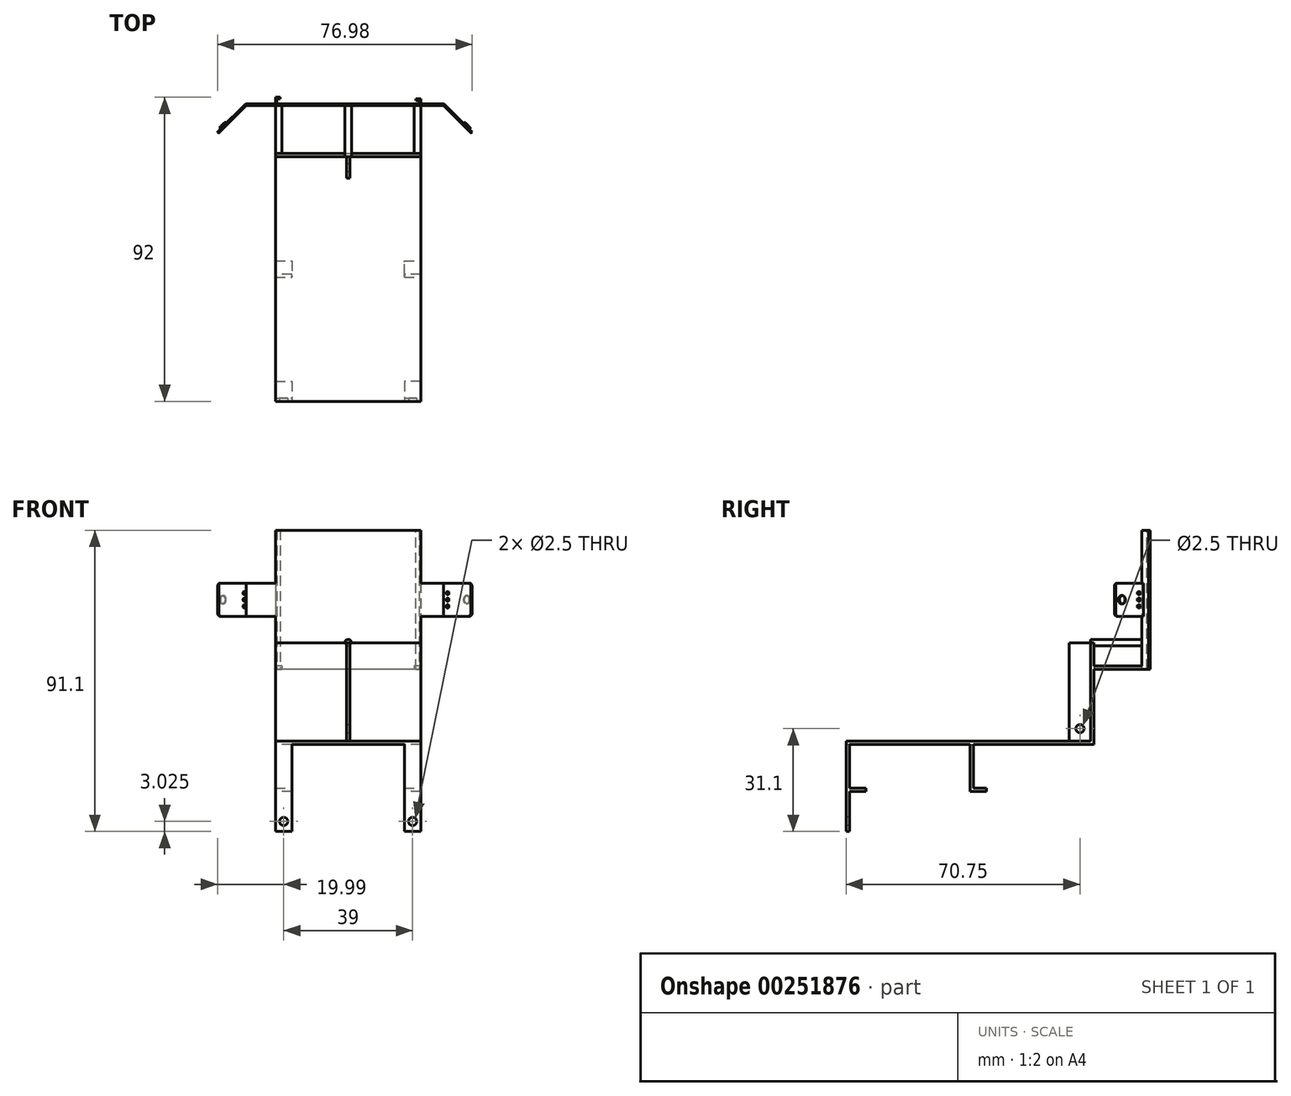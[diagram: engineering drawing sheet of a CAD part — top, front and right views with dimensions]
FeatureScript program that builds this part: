
annotation { "Feature Type Name" : "Feature", "Feature Type Description" : "" }
export const myFeature = defineFeature(function(context is Context, id is Id, definition is map)
    precondition{}
    {
        {
            var Q0;
            Q0=qCreatedBy(makeId("Front.planeOp"),FACE);
            var sketch = newSketch(context, id + "F0", { "sketchPlane" : qUnion([Q0])});
            skLineSegment(sketch, "E0", {"start": v(-30, 5) * mm, "end": v(30, 5) * mm});
            skLineSegment(sketch, "E1", {"start": v(30, 5) * mm, "end": v(30, -5) * mm});
            skLineSegment(sketch, "E2", {"start": v(30, -5) * mm, "end": v(-30, -5) * mm});
            skLineSegment(sketch, "E3", {"start": v(-30, -5) * mm, "end": v(-30, 5) * mm});
            skLineSegment(sketch, "E4", {"start": v(0, 5) * mm, "end": v(-21, 5) * mm, "construction": true});
            skLineSegment(sketch, "E5", {"start": v(-21, 5) * mm, "end": v(-21, 21) * mm, "construction": true});
            skLineSegment(sketch, "E6", {"start": v(-21, 21) * mm, "end": v(23, 21) * mm});
            skLineSegment(sketch, "E7", {"start": v(23, 21) * mm, "end": v(23, -21) * mm});
            skLineSegment(sketch, "E8", {"start": v(23, -21) * mm, "end": v(-21, -21) * mm});
            skLineSegment(sketch, "E9", {"start": v(-21, -21) * mm, "end": v(-21, 21) * mm});
            skPoint(sketch, "E10", {"position": v(0, 0) * mm});
            skLineSegment(sketch, "E11", {"start": v(-21, -21) * mm, "end": v(23, -5) * mm, "construction": true});
            skLineSegment(sketch, "E12", {"start": v(-21, -5) * mm, "end": v(23, -21) * mm, "construction": true});
            skPoint(sketch, "E13", {"position": v(1, -13) * mm});
            skCircle(sketch, "E14", {"center": v(1, -13) * mm, "radius": 1 * mm});
            skSolve(sketch);
        }
        {
            var Q0;
            Q0 = qSketchRegion(id + "F0", true);
            extrude(context, id + "F1", {"entities" : qUnion([Q0]), "depth" : 0.5 * mm});
        }
        {
            var Q0;
            Q0=makeQuery(id+"F1.opExtrude","CAP_EDGE",EDGE,{"disambiguationData":[OSD([sQuery(id+"F0.wireOp",EDGE,"E1")])],"isStart":true});
            var Q1;
            Q1=makeQuery(id+"F1.opExtrude","SWEPT_FACE",FACE,{"disambiguationData":[OSD([sQuery(id+"F0.wireOp",EDGE,"E1")])]});
            cPlane(context, id + "F2", {"entities" : qUnion([Q0, Q1]), "cplaneType" : CPlaneType.LINE_ANGLE, "offset" : 25 * mm, "angle" : 45 * degree, "oppositeDirection" : true, "width" : 150 * mm, "height" : 150 * mm});
        }
        {
            var Q0;
            Q0=qCreatedBy(id+"F2.planeOp",FACE);
            var sketch = newSketch(context, id + "F3", { "sketchPlane" : qUnion([Q0])});
            skLineSegment(sketch, "E15.0.0", {"start": v(21.21, -5) * mm, "end": v(21.21, 5) * mm});
            skLineSegment(sketch, "E15.0.1", {"start": v(21.21, 5) * mm, "end": v(21.57, 5) * mm});
            skLineSegment(sketch, "E15.0.2", {"start": v(21.57, 5) * mm, "end": v(21.57, -5) * mm});
            skLineSegment(sketch, "E15.0.3", {"start": v(21.57, -5) * mm, "end": v(21.21, -5) * mm});
            skLineSegment(sketch, "E16", {"start": v(21.21, -5) * mm, "end": v(32.21, -5) * mm});
            skLineSegment(sketch, "E17", {"start": v(33.21, -4) * mm, "end": v(33.21, 4) * mm});
            skLineSegment(sketch, "E18", {"start": v(32.21, 5) * mm, "end": v(21.21, 5) * mm});
            skPoint(sketch, "E19.visualSharp", {"position": v(33.21, 5) * mm});
            skArc(sketch, "E19.filletArc", {"start": v(33.21, 4) * mm, "mid": v(32.92, 4.7) * mm, "end": v(32.21, 5) * mm});
            skPoint(sketch, "E20.visualSharp", {"position": v(21.21, 5) * mm});
            skLineSegment(sketch, "E20.filletArc", {"start": v(21.21, 5) * mm, "end": v(21.21, 5) * mm});
            skPoint(sketch, "E21.visualSharp", {"position": v(21.21, -5) * mm});
            skLineSegment(sketch, "E21.filletArc", {"start": v(21.21, -5) * mm, "end": v(21.21, -5) * mm});
            skPoint(sketch, "E22.visualSharp", {"position": v(33.21, -5) * mm});
            skArc(sketch, "E22.filletArc", {"start": v(32.21, -5) * mm, "mid": v(32.92, -4.7) * mm, "end": v(33.21, -4) * mm});
            skLineSegment(sketch, "E23", {"start": v(21.21, -5) * mm, "end": v(23.21, -5) * mm, "construction": true});
            skLineSegment(sketch, "E24", {"start": v(23.21, -5) * mm, "end": v(23.21, -2) * mm, "construction": true});
            skLineSegment(sketch, "E25", {"start": v(23.21, -2) * mm, "end": v(23.21, 0) * mm, "construction": true});
            skLineSegment(sketch, "E26", {"start": v(23.21, 0) * mm, "end": v(23.21, 2) * mm, "construction": true});
            skCircle(sketch, "E27", {"center": v(23.21, 2) * mm, "radius": 0.5 * mm});
            skCircle(sketch, "E28", {"center": v(23.21, 0) * mm, "radius": 0.5 * mm});
            skCircle(sketch, "E29", {"center": v(23.21, -2) * mm, "radius": 0.5 * mm});
            skSolve(sketch);
        }
        {
            var Q0;
            {var subQ0=sQuery(id+"F3.wireOp",EDGE,"E15.0.2");Q0=makeQuery(id+"F3.imprint","IMPRINT",FACE,{"disambiguationData":[TD([[makeQuery(id+"F3.imprint","IMPRINT",EDGE,{"derivedFrom":subQ0}),1.0]])]});}
            var Q1;
            {var subQ0=sQuery(id+"F3.wireOp",EDGE,"E15.0.0");Q1=makeQuery(id+"F3.imprint","IMPRINT",FACE,{"disambiguationData":[TD([[makeQuery(id+"F3.imprint","IMPRINT",EDGE,{"derivedFrom":subQ0}),-1.0]])]});}
            extrude(context, id + "F4", {"entities" : qUnion([Q0, Q1]), "operationType" : NewBodyOperationType.ADD, "depth" : 0.5 * mm});
        }
        {
            var Q0;
            Q0=makeQuery(id+"F1.opExtrude","CAP_EDGE",EDGE,{"disambiguationData":[OSD([sQuery(id+"F0.wireOp",EDGE,"E3")])],"isStart":true});
            var Q1;
            Q1=makeQuery(id+"F1.opExtrude","SWEPT_FACE",FACE,{"disambiguationData":[OSD([sQuery(id+"F0.wireOp",EDGE,"E3")])]});
            cPlane(context, id + "F5", {"entities" : qUnion([Q0, Q1]), "cplaneType" : CPlaneType.LINE_ANGLE, "offset" : 25 * mm, "angle" : 45 * degree, "oppositeDirection" : true, "width" : 150 * mm, "height" : 150 * mm});
        }
        {
            var Q0;
            Q0=qCreatedBy(id+"F5.planeOp",FACE);
            var sketch = newSketch(context, id + "F6", { "sketchPlane" : qUnion([Q0])});
            skLineSegment(sketch, "E30.0.0", {"start": v(-21.21, 5) * mm, "end": v(-21.21, -5) * mm});
            skLineSegment(sketch, "E30.0.1", {"start": v(-21.21, -5) * mm, "end": v(-21.57, -5) * mm});
            skLineSegment(sketch, "E30.0.2", {"start": v(-21.57, -5) * mm, "end": v(-21.57, 5) * mm});
            skLineSegment(sketch, "E30.0.3", {"start": v(-21.57, 5) * mm, "end": v(-21.21, 5) * mm});
            skLineSegment(sketch, "E31", {"start": v(-21.21, -5) * mm, "end": v(-32.21, -5) * mm});
            skLineSegment(sketch, "E32", {"start": v(-33.21, -4) * mm, "end": v(-33.21, 4) * mm});
            skLineSegment(sketch, "E33", {"start": v(-32.21, 5) * mm, "end": v(-21.21, 5) * mm});
            skPoint(sketch, "E34.visualSharp", {"position": v(-33.21, -5) * mm});
            skArc(sketch, "E34.filletArc", {"start": v(-33.21, -4) * mm, "mid": v(-32.92, -4.7) * mm, "end": v(-32.21, -5) * mm});
            skPoint(sketch, "E35.visualSharp", {"position": v(-33.21, 5) * mm});
            skArc(sketch, "E35.filletArc", {"start": v(-32.21, 5) * mm, "mid": v(-32.92, 4.7) * mm, "end": v(-33.21, 4) * mm});
            skLineSegment(sketch, "E36", {"start": v(-21.21, -5) * mm, "end": v(-22.21, -5) * mm, "construction": true});
            skLineSegment(sketch, "E37", {"start": v(-22.21, -5) * mm, "end": v(-22.21, -2) * mm, "construction": true});
            skLineSegment(sketch, "E38", {"start": v(-22.21, -2) * mm, "end": v(-22.21, 0) * mm, "construction": true});
            skLineSegment(sketch, "E39", {"start": v(-22.21, 0) * mm, "end": v(-22.21, 2) * mm, "construction": true});
            skCircle(sketch, "E40", {"center": v(-22.21, 2) * mm, "radius": 0.5 * mm});
            skCircle(sketch, "E41", {"center": v(-22.21, 0) * mm, "radius": 0.5 * mm});
            skCircle(sketch, "E42", {"center": v(-22.21, -2) * mm, "radius": 0.5 * mm});
            skPoint(sketch, "E43.endSnap0", {"position": v(-33.21, 0) * mm});
            skSolve(sketch);
        }
        {
            var Q0;
            {var subQ0=sQuery(id+"F6.wireOp",EDGE,"E30.0.2");Q0=makeQuery(id+"F6.imprint","IMPRINT",FACE,{"disambiguationData":[TD([[makeQuery(id+"F6.imprint","IMPRINT",EDGE,{"derivedFrom":subQ0}),1.0]])]});}
            var Q1;
            {var subQ0=sQuery(id+"F6.wireOp",EDGE,"E30.0.0");Q1=makeQuery(id+"F6.imprint","IMPRINT",FACE,{"disambiguationData":[TD([[makeQuery(id+"F6.imprint","IMPRINT",EDGE,{"derivedFrom":subQ0}),-1.0]])]});}
            extrude(context, id + "F7", {"entities" : qUnion([Q0, Q1]), "operationType" : NewBodyOperationType.ADD, "depth" : 0.5 * mm});
        }
        {
            var Q0;
            Q0=makeQuery(id+"F4.opExtrude","CAP_FACE",FACE,{"disambiguationData":[OSD([sQuery(id+"F3.wireOp",EDGE,"E15.0.0"),sQuery(id+"F3.wireOp",EDGE,"E16"),sQuery(id+"F3.wireOp",EDGE,"E17"),sQuery(id+"F3.wireOp",EDGE,"E18"),sQuery(id+"F3.wireOp",EDGE,"E19.filletArc"),sQuery(id+"F3.wireOp",EDGE,"E22.filletArc"),sQuery(id+"F3.wireOp",EDGE,"E27"),sQuery(id+"F3.wireOp",EDGE,"E28"),sQuery(id+"F3.wireOp",EDGE,"E29")])],"isStart":true});
            var sketch = newSketch(context, id + "F8", { "sketchPlane" : qUnion([Q0])});
            skLineSegment(sketch, "E44.0", {"start": v(-33.21, -4) * mm, "end": v(-33.21, 4) * mm});
            skLineSegment(sketch, "E45", {"start": v(-33.21, 0) * mm, "end": v(-30.76, 0) * mm, "construction": true});
            skCircle(sketch, "E46", {"center": v(-30.76, 0) * mm, "radius": 1.25 * mm});
            skSolve(sketch);
        }
        {
            var Q0;
            Q0=makeQuery(id+"F8.imprint","IMPRINT",FACE,{"disambiguationData":[TD([[makeQuery(id+"F8.imprint","IMPRINT",EDGE,{"derivedFrom":sQuery(id+"F8.wireOp",EDGE,"E46")}),1.0]])]});
            extrude(context, id + "F9", {"entities" : qUnion([Q0]), "operationType" : NewBodyOperationType.ADD, "depth" : 0.5 * mm});
        }
        {
            var Q0;
            Q0=makeQuery(id+"F7.opExtrude","CAP_FACE",FACE,{"disambiguationData":[OSD([sQuery(id+"F6.wireOp",EDGE,"E30.0.0"),sQuery(id+"F6.wireOp",EDGE,"E31"),sQuery(id+"F6.wireOp",EDGE,"E32"),sQuery(id+"F6.wireOp",EDGE,"E33"),sQuery(id+"F6.wireOp",EDGE,"E34.filletArc"),sQuery(id+"F6.wireOp",EDGE,"E35.filletArc"),sQuery(id+"F6.wireOp",EDGE,"E40"),sQuery(id+"F6.wireOp",EDGE,"E41"),sQuery(id+"F6.wireOp",EDGE,"E42")])],"isStart":true});
            var sketch = newSketch(context, id + "F10", { "sketchPlane" : qUnion([Q0])});
            skLineSegment(sketch, "E47.0", {"start": v(33.21, -4) * mm, "end": v(33.21, 4) * mm});
            skLineSegment(sketch, "E48", {"start": v(33.21, 0) * mm, "end": v(30.76, 0) * mm, "construction": true});
            skCircle(sketch, "E49", {"center": v(30.76, 0) * mm, "radius": 1.25 * mm});
            skSolve(sketch);
        }
        {
            var Q0;
            Q0=makeQuery(id+"F10.imprint","IMPRINT",FACE,{"disambiguationData":[TD([[makeQuery(id+"F10.imprint","IMPRINT",EDGE,{"derivedFrom":sQuery(id+"F10.wireOp",EDGE,"E49")}),1.0]])]});
            extrude(context, id + "F11", {"entities" : qUnion([Q0]), "operationType" : NewBodyOperationType.ADD, "depth" : 0.5 * mm});
        }
        {
            var Q0;
            {var subQ5=sQuery(id+"F0.wireOp",EDGE,"E6");Q0=makeQuery(id+"F0.imprint","IMPRINT",FACE,{"disambiguationData":[TD([[makeQuery(id+"F0.imprint","IMPRINT",EDGE,{"derivedFrom":subQ5}),-1.0]])]});}
            var Q1;
            {var subQ5=sQuery(id+"F0.wireOp",EDGE,"E8");Q1=makeQuery(id+"F0.imprint","IMPRINT",FACE,{"disambiguationData":[TD([[makeQuery(id+"F0.imprint","IMPRINT",EDGE,{"derivedFrom":subQ5}),-1.0]])]});}
            extrude(context, id + "F12", {"entities" : qUnion([Q0, Q1]), "operationType" : NewBodyOperationType.ADD, "depth" : 0.5 * mm});
        }
        {
            var Q0;
            Q0=makeQuery(id+"F1.opExtrude","SWEPT_FACE",FACE,{"disambiguationData":[OSD([sQuery(id+"F0.wireOp",EDGE,"E8")])]});
            var sketch = newSketch(context, id + "F13", { "sketchPlane" : qUnion([Q0])});
            skLineSegment(sketch, "E50.0.0", {"start": v(-21, 0) * mm, "end": v(23, 0) * mm});
            skLineSegment(sketch, "E50.0.1", {"start": v(23, 0) * mm, "end": v(23, 0.5) * mm});
            skLineSegment(sketch, "E50.0.2", {"start": v(23, 0.5) * mm, "end": v(-21, 0.5) * mm});
            skLineSegment(sketch, "E50.0.3", {"start": v(-21, 0.5) * mm, "end": v(-21, 0) * mm});
            skLineSegment(sketch, "E51", {"start": v(23, 0) * mm, "end": v(23, 15) * mm});
            skLineSegment(sketch, "E52", {"start": v(-21, 15) * mm, "end": v(-21, 0) * mm});
            skLineSegment(sketch, "E53", {"start": v(23, 15) * mm, "end": v(21, 15) * mm});
            skLineSegment(sketch, "E54", {"start": v(21, 15) * mm, "end": v(21, 0) * mm});
            skLineSegment(sketch, "E55", {"start": v(-21, 15) * mm, "end": v(-19, 15) * mm});
            skLineSegment(sketch, "E56", {"start": v(-19, 15) * mm, "end": v(-19, 0) * mm});
            skSolve(sketch);
        }
        {
            var Q0;
            Q0=makeQuery(id+"F0.imprint","IMPRINT",FACE,{"disambiguationData":[TD([[makeQuery(id+"F0.imprint","IMPRINT",EDGE,{"derivedFrom":sQuery(id+"F0.wireOp",EDGE,"E14")}),1.0]])]});
            extrude(context, id + "F14", {"entities" : qUnion([Q0]), "operationType" : NewBodyOperationType.ADD, "depth" : 15 * mm});
        }
        {
            var Q0;
            {var subQ5=sQuery(id+"F13.wireOp",EDGE,"E55");Q0=makeQuery(id+"F13.imprint","IMPRINT",FACE,{"disambiguationData":[TD([[makeQuery(id+"F13.imprint","IMPRINT",EDGE,{"derivedFrom":subQ5}),-1.0]])]});}
            var Q1;
            {var subQ5=sQuery(id+"F13.wireOp",EDGE,"E53");Q1=makeQuery(id+"F13.imprint","IMPRINT",FACE,{"disambiguationData":[TD([[makeQuery(id+"F13.imprint","IMPRINT",EDGE,{"derivedFrom":subQ5}),1.0]])]});}
            extrude(context, id + "F15", {"entities" : qUnion([Q0, Q1]), "operationType" : NewBodyOperationType.ADD, "oppositeDirection" : true, "depth" : 1 * mm});
        }
        {
            var Q0;
            Q0=makeQuery(id+"F14.opExtrude","CAP_FACE",FACE,{"disambiguationData":[OSD([sQuery(id+"F0.wireOp",EDGE,"E14")])],"isStart":false});
            var sketch = newSketch(context, id + "F16", { "sketchPlane" : qUnion([Q0])});
            skLineSegment(sketch, "E57.0.0", {"start": v(-21, -21) * mm, "end": v(-19, -21) * mm});
            skLineSegment(sketch, "E57.0.1", {"start": v(-19, -21) * mm, "end": v(-19, -20) * mm});
            skLineSegment(sketch, "E57.0.2", {"start": v(-19, -20) * mm, "end": v(-21, -20) * mm});
            skLineSegment(sketch, "E57.0.3", {"start": v(-21, -20) * mm, "end": v(-21, -21) * mm});
            skLineSegment(sketch, "E58.0.0", {"start": v(21, -21) * mm, "end": v(23, -21) * mm});
            skLineSegment(sketch, "E58.0.1", {"start": v(23, -21) * mm, "end": v(23, -20) * mm});
            skLineSegment(sketch, "E58.0.2", {"start": v(23, -20) * mm, "end": v(21, -20) * mm});
            skLineSegment(sketch, "E58.0.3", {"start": v(21, -20) * mm, "end": v(21, -21) * mm});
            skLineSegment(sketch, "E59", {"start": v(0, -13) * mm, "end": v(-21, -13) * mm, "construction": true});
            skLineSegment(sketch, "E60", {"start": v(0, -13) * mm, "end": v(23, -13) * mm, "construction": true});
            skLineSegment(sketch, "E61", {"start": v(-21, -13) * mm, "end": v(-21, -42.75) * mm});
            skLineSegment(sketch, "E62", {"start": v(-21, -42.75) * mm, "end": v(23, -42.75) * mm});
            skLineSegment(sketch, "E63", {"start": v(23, -42.75) * mm, "end": v(23, -13) * mm});
            skLineSegment(sketch, "E64", {"start": v(23, -13) * mm, "end": v(-21, -13) * mm});
            skSolve(sketch);
        }
        {
            var Q0;
            {var subQ5=sQuery(id+"F16.wireOp",EDGE,"E57.0.0");Q0=makeQuery(id+"F16.imprint","IMPRINT",FACE,{"disambiguationData":[TD([[makeQuery(id+"F16.imprint","IMPRINT",EDGE,{"derivedFrom":subQ5}),-1.0]])]});}
            var Q1;
            {var subQ0=sQuery(id+"F16.wireOp",EDGE,"E57.0.0");Q1=makeQuery(id+"F16.imprint","IMPRINT",FACE,{"disambiguationData":[TD([[makeQuery(id+"F16.imprint","IMPRINT",EDGE,{"derivedFrom":subQ0}),1.0]])]});}
            var Q2;
            Q2=makeQuery(id+"F16.imprint","IMPRINT",FACE,{"disambiguationData":[TD([[makeQuery(id+"F16.imprint","IMPRINT",EDGE,{"derivedFrom":makeQuery(id+"F14.opExtrude","CAP_EDGE",EDGE,{"disambiguationData":[OSD([sQuery(id+"F0.wireOp",EDGE,"E14")])],"isStart":false})}),1.0]])]});
            var Q3;
            {var subQ0=sQuery(id+"F16.wireOp",EDGE,"E58.0.0");Q3=makeQuery(id+"F16.imprint","IMPRINT",FACE,{"disambiguationData":[TD([[makeQuery(id+"F16.imprint","IMPRINT",EDGE,{"derivedFrom":subQ0}),1.0]])]});}
            extrude(context, id + "F17", {"entities" : qUnion([Q0, Q1, Q2, Q3]), "operationType" : NewBodyOperationType.ADD, "depth" : 1 * mm});
        }
        {
            var Q0;
            Q0=makeQuery(id+"F17.opExtrude","CAP_FACE",FACE,{"disambiguationData":[OSD([sQuery(id+"F16.wireOp",EDGE,"E61"),sQuery(id+"F16.wireOp",EDGE,"E62"),sQuery(id+"F16.wireOp",EDGE,"E63"),sQuery(id+"F16.wireOp",EDGE,"E64")])],"isStart":false});
            var sketch = newSketch(context, id + "F18", { "sketchPlane" : qUnion([Q0])});
            skLineSegment(sketch, "E65", {"start": v(1, -42.75) * mm, "end": v(0.5, -42.75) * mm, "construction": true});
            skLineSegment(sketch, "E66", {"start": v(0.5, -42.75) * mm, "end": v(0.5, -13) * mm});
            skLineSegment(sketch, "E67", {"start": v(0.5, -13) * mm, "end": v(1.5, -13) * mm});
            skLineSegment(sketch, "E68", {"start": v(1.5, -13) * mm, "end": v(1.5, -42.75) * mm});
            skLineSegment(sketch, "E69", {"start": v(1.5, -42.75) * mm, "end": v(0.5, -42.75) * mm});
            skSolve(sketch);
        }
        {
            var Q0;
            Q0=makeQuery(id+"F18.imprint","IMPRINT",FACE,{"disambiguationData":[TD([[makeQuery(id+"F18.imprint","IMPRINT",EDGE,{"derivedFrom":sQuery(id+"F18.wireOp",EDGE,"E66")}),-1.0]])]});
            extrude(context, id + "F19", {"entities" : qUnion([Q0]), "operationType" : NewBodyOperationType.ADD, "depth" : 6.5 * mm});
        }
        {
            var Q0;
            Q0=makeQuery(id+"F19.opExtrude","SWEPT_FACE",FACE,{"disambiguationData":[OSD([sQuery(id+"F18.wireOp",EDGE,"E68")])]});
            var sketch = newSketch(context, id + "F20", { "sketchPlane" : qUnion([Q0])});
            skLineSegment(sketch, "E70", {"start": v(-16, -42.75) * mm, "end": v(-16, -39) * mm, "construction": true});
            skLineSegment(sketch, "E71", {"start": v(-16, -39) * mm, "end": v(-19.25, -39) * mm, "construction": true});
            skPoint(sketch, "E72", {"position": v(-19.25, -39) * mm});
            skLineSegment(sketch, "E73", {"start": v(-22.5, -13) * mm, "end": v(-22.5, -16) * mm, "construction": true});
            skLineSegment(sketch, "E74", {"start": v(-19.25, -39) * mm, "end": v(-19.25, -13) * mm, "construction": true});
            skLineSegment(sketch, "E75", {"start": v(-19.25, -39) * mm, "end": v(-77.45, -39) * mm, "construction": true});
            skLineSegment(sketch, "E76", {"start": v(-22.5, -13) * mm, "end": v(-80.7, -13) * mm});
            skLineSegment(sketch, "E77", {"start": v(-80.7, -13) * mm, "end": v(-80.7, -42.75) * mm});
            skLineSegment(sketch, "E78", {"start": v(-80.7, -42.75) * mm, "end": v(-74.7, -42.75) * mm});
            skLineSegment(sketch, "E79", {"start": v(-74.7, -42.75) * mm, "end": v(-74.7, -16) * mm});
            skLineSegment(sketch, "E80", {"start": v(-74.7, -16) * mm, "end": v(-22.5, -16) * mm});
            skLineSegment(sketch, "E81", {"start": v(-80.7, -13) * mm, "end": v(-80.7, 13.63) * mm});
            skLineSegment(sketch, "E82", {"start": v(-80.7, 13.63) * mm, "end": v(-74.7, 13.63) * mm});
            skLineSegment(sketch, "E83", {"start": v(-74.7, 13.63) * mm, "end": v(-74.7, -13) * mm});
            skLineSegment(sketch, "E84", {"start": v(-77.45, -39) * mm, "end": v(-77.45, 10.24) * mm, "construction": true});
            skPoint(sketch, "E85", {"position": v(-77.45, -39) * mm});
            skPoint(sketch, "E86", {"position": v(-77.45, 10.24) * mm});
            skLineSegment(sketch, "E87", {"start": v(-74.7, -16) * mm, "end": v(-80.7, -16) * mm, "construction": true});
            skLineSegment(sketch, "E88", {"start": v(-80.7, -16) * mm, "end": v(-80.7, -13) * mm, "construction": true});
            skLineSegment(sketch, "E89", {"start": v(-22.5, -14.5) * mm, "end": v(-80.7, -14.5) * mm, "construction": true});
            skSolve(sketch);
        }
        {
            var Q0;
            Q0=sQuery(id+"F20.wireOp",VERTEX,"E72");
            var Q1;
            Q1=makeQuery(id+"F1.opExtrude","SWEPT_BODY",BODY,{"disambiguationData":[OSD([sQuery(id+"F0.wireOp",EDGE,"E0"),sQuery(id+"F0.wireOp",EDGE,"E1"),sQuery(id+"F0.wireOp",EDGE,"E2"),sQuery(id+"F0.wireOp",EDGE,"E3"),sQuery(id+"F0.wireOp",EDGE,"E6"),sQuery(id+"F0.wireOp",EDGE,"E7"),sQuery(id+"F0.wireOp",EDGE,"E8"),sQuery(id+"F0.wireOp",EDGE,"E9"),sQuery(id+"F0.wireOp",EDGE,"E14")])]});
            hole(context, id + "F21", {"style" : HoleStyle.SIMPLE, "endStyle" : HoleEndStyle.BLIND, "holeDiameter" : 2.5 * mm, "holeDepth" : 8 * mm, "tappedDepth" : 12 * mm, "tapClearance" : 3, "locations" : qUnion([Q0]), "scope" : qUnion([Q1])});
        }
        {
            var Q0;
            Q0=makeQuery(id+"F19.boolean.opBoolean","MERGE",FACE,{"derivedFrom":[makeQuery(id+"F17.opExtrude","SWEPT_FACE",FACE,{"disambiguationData":[OSD([sQuery(id+"F16.wireOp",EDGE,"E62")])]}),makeQuery(id+"F19.opExtrude","SWEPT_FACE",FACE,{"disambiguationData":[OSD([sQuery(id+"F18.wireOp",EDGE,"E69")])]})]});
            var sketch = newSketch(context, id + "F22", { "sketchPlane" : qUnion([Q0])});
            skPoint(sketch, "E90.0", {"position": v(1.5, 74.7) * mm});
            skPoint(sketch, "E91.0", {"position": v(1.5, 80.7) * mm});
            skLineSegment(sketch, "E92", {"start": v(23, 15) * mm, "end": v(23, 90) * mm});
            skLineSegment(sketch, "E93", {"start": v(23, 90) * mm, "end": v(-21, 90) * mm});
            skLineSegment(sketch, "E94", {"start": v(-21, 90) * mm, "end": v(-21, 15) * mm});
            skLineSegment(sketch, "E95", {"start": v(23, 90) * mm, "end": v(23, 52.5) * mm, "construction": true});
            skLineSegment(sketch, "E96", {"start": v(23, 90) * mm, "end": v(23, 52) * mm, "construction": true});
            skLineSegment(sketch, "E97", {"start": v(23, 52) * mm, "end": v(-21, 52) * mm, "construction": true});
            skLineSegment(sketch, "E98", {"start": v(23, 52) * mm, "end": v(23, 51.5) * mm});
            skLineSegment(sketch, "E99", {"start": v(23, 53) * mm, "end": v(23, 52.5) * mm});
            skLineSegment(sketch, "E100", {"start": v(-21, 52) * mm, "end": v(-21, 52.5) * mm});
            skLineSegment(sketch, "E101", {"start": v(-21, 52.5) * mm, "end": v(-21, 52.5) * mm});
            skLineSegment(sketch, "E102", {"start": v(23, 51.5) * mm, "end": v(18, 51.5) * mm});
            skLineSegment(sketch, "E103", {"start": v(18, 51.5) * mm, "end": v(18, 52.5) * mm});
            skLineSegment(sketch, "E104", {"start": v(18, 52.5) * mm, "end": v(23, 52.5) * mm});
            skLineSegment(sketch, "E105", {"start": v(23, 52.5) * mm, "end": v(23, 51.5) * mm});
            skLineSegment(sketch, "E106", {"start": v(-21, 52) * mm, "end": v(-21, 52.5) * mm, "construction": true});
            skLineSegment(sketch, "E107", {"start": v(-21, 52.5) * mm, "end": v(-16, 52.5) * mm});
            skLineSegment(sketch, "E108", {"start": v(-16, 52.5) * mm, "end": v(-16, 51.5) * mm});
            skLineSegment(sketch, "E109", {"start": v(-16, 51.5) * mm, "end": v(-21, 51.5) * mm});
            skLineSegment(sketch, "E110", {"start": v(-21, 51.5) * mm, "end": v(-21, 52.5) * mm});
            skSolve(sketch);
        }
        {
            var Q0;
            {var subQ8=sQuery(id+"F22.wireOp",EDGE,"60eaaffc-4cc3-488e-9d33-9b9b55c51e88.0.0");Q0=makeQuery(id+"F22.imprint","IMPRINT",FACE,{"disambiguationData":[TD([[makeQuery(id+"F22.imprint","IMPRINT",EDGE,{"derivedFrom":subQ8}),-1.0]])]});}
            var Q1;
            {var subQ0=sQuery(id+"F22.wireOp",EDGE,"60eaaffc-4cc3-488e-9d33-9b9b55c51e88.0.0");Q1=makeQuery(id+"F22.imprint","IMPRINT",FACE,{"disambiguationData":[TD([[makeQuery(id+"F22.imprint","IMPRINT",EDGE,{"derivedFrom":subQ0}),1.0]])]});}
            var Q2;
            {var subQ1=sQuery(id+"F16.wireOp",EDGE,"E62");var subQ2=makeQuery(id+"F17.opExtrude","CAP_EDGE",EDGE,{"disambiguationData":[OSD([subQ1])],"isStart":true});Q2=makeQuery(id+"F22.imprint","IMPRINT",FACE,{"disambiguationData":[TD([[makeQuery(id+"F22.imprint","IMPRINT",EDGE,{"derivedFrom":subQ2}),1.0]])]});}
            extrude(context, id + "F23", {"entities" : qUnion([Q0, Q1, Q2]), "operationType" : NewBodyOperationType.ADD, "depth" : 1 * mm});
        }
        {
            var Q0;
            Q0=sQuery(id+"F20.wireOp",VERTEX,"E85");
            var Q1;
            Q1=sQuery(id+"F20.wireOp",VERTEX,"E86");
            var Q2;
            Q2=makeQuery(id+"F1.opExtrude","SWEPT_BODY",BODY,{"disambiguationData":[OSD([sQuery(id+"F0.wireOp",EDGE,"E0"),sQuery(id+"F0.wireOp",EDGE,"E1"),sQuery(id+"F0.wireOp",EDGE,"E2"),sQuery(id+"F0.wireOp",EDGE,"E3"),sQuery(id+"F0.wireOp",EDGE,"E6"),sQuery(id+"F0.wireOp",EDGE,"E7"),sQuery(id+"F0.wireOp",EDGE,"E8"),sQuery(id+"F0.wireOp",EDGE,"E9"),sQuery(id+"F0.wireOp",EDGE,"E14")])]});
            hole(context, id + "F24", {"style" : HoleStyle.SIMPLE, "endStyle" : HoleEndStyle.BLIND, "holeDiameter" : 2.5 * mm, "holeDepth" : 8 * mm, "tappedDepth" : 12 * mm, "tapClearance" : 3, "locations" : qUnion([Q0, Q1]), "scope" : qUnion([Q2])});
        }
        {
            var Q0;
            {var subQ14=sQuery(id+"F22.wireOp",EDGE,"E93");Q0=makeQuery(id+"F22.imprint","IMPRINT",FACE,{"disambiguationData":[TD([[makeQuery(id+"F22.imprint","IMPRINT",EDGE,{"derivedFrom":subQ14}),1.0]])]});}
            var Q1;
            {var subQ2=sQuery(id+"F16.wireOp",EDGE,"E62");var subQ3=makeQuery(id+"F17.opExtrude","CAP_EDGE",EDGE,{"disambiguationData":[OSD([subQ2])],"isStart":true});Q1=makeQuery(id+"F22.imprint","IMPRINT",FACE,{"disambiguationData":[TD([[makeQuery(id+"F22.imprint","IMPRINT",EDGE,{"derivedFrom":subQ3}),1.0]])]});}
            extrude(context, id + "F25", {"entities" : qUnion([Q0, Q1]), "operationType" : NewBodyOperationType.ADD, "depth" : 1 * mm});
        }
        {
            var Q0;
            Q0=makeQuery(id+"F25.opExtrude","SWEPT_FACE",FACE,{"disambiguationData":[OSD([sQuery(id+"F22.wireOp",EDGE,"E93")])]});
            var sketch = newSketch(context, id + "F26", { "sketchPlane" : qUnion([Q0])});
            skLineSegment(sketch, "E111", {"start": v(-21, -42.75) * mm, "end": v(-21, -58) * mm});
            skLineSegment(sketch, "E112", {"start": v(-21, -58) * mm, "end": v(-21, -70.1) * mm});
            skLineSegment(sketch, "E113", {"start": v(-21, -70.1) * mm, "end": v(-16, -70.1) * mm});
            skLineSegment(sketch, "E114", {"start": v(-16, -70.1) * mm, "end": v(-16, -42.75) * mm});
            skLineSegment(sketch, "E115", {"start": v(23, -42.75) * mm, "end": v(23, -58) * mm});
            skLineSegment(sketch, "E116", {"start": v(23, -58) * mm, "end": v(23, -70.1) * mm});
            skLineSegment(sketch, "E117", {"start": v(23, -70.1) * mm, "end": v(18, -70.1) * mm});
            skLineSegment(sketch, "E118", {"start": v(18, -70.1) * mm, "end": v(18, -42.75) * mm});
            skLineSegment(sketch, "E119", {"start": v(-16, -70.1) * mm, "end": v(-21, -64.05) * mm, "construction": true});
            skLineSegment(sketch, "E120", {"start": v(-21, -70.1) * mm, "end": v(-16, -64.05) * mm, "construction": true});
            skCircle(sketch, "E121", {"center": v(-18.5, -67.07) * mm, "radius": 1.25 * mm});
            skLineSegment(sketch, "E122", {"start": v(18, -70.1) * mm, "end": v(23, -64.05) * mm, "construction": true});
            skLineSegment(sketch, "E123", {"start": v(23, -70.1) * mm, "end": v(18, -64.05) * mm, "construction": true});
            skCircle(sketch, "E124", {"center": v(20.5, -67.07) * mm, "radius": 1.25 * mm});
            skSolve(sketch);
        }
        {
            var Q0;
            {var subQ4=sQuery(id+"F26.wireOp",EDGE,"E112");Q0=makeQuery(id+"F26.imprint","IMPRINT",FACE,{"disambiguationData":[TD([[makeQuery(id+"F26.imprint","IMPRINT",EDGE,{"derivedFrom":subQ4}),1.0]])]});}
            var Q1;
            {var subQ4=sQuery(id+"F26.wireOp",EDGE,"E116");Q1=makeQuery(id+"F26.imprint","IMPRINT",FACE,{"disambiguationData":[TD([[makeQuery(id+"F26.imprint","IMPRINT",EDGE,{"derivedFrom":subQ4}),-1.0]])]});}
            extrude(context, id + "F27", {"entities" : qUnion([Q0, Q1]), "operationType" : NewBodyOperationType.ADD, "oppositeDirection" : true, "depth" : 1 * mm});
        }
        {
            var Q0;
            Q0=makeQuery(id+"F27.opExtrude","CAP_FACE",FACE,{"disambiguationData":[OSD([sQuery(id+"F22.wireOp",EDGE,"E93"),sQuery(id+"F26.wireOp",EDGE,"E115"),sQuery(id+"F26.wireOp",EDGE,"E116"),sQuery(id+"F26.wireOp",EDGE,"E117"),sQuery(id+"F26.wireOp",EDGE,"E118"),sQuery(id+"F26.wireOp",EDGE,"E124")])],"isStart":false});
            var sketch = newSketch(context, id + "F28", { "sketchPlane" : qUnion([Q0])});
            skLineSegment(sketch, "E125", {"start": v(-23, -43.75) * mm, "end": v(-23, -58) * mm, "construction": true});
            skLineSegment(sketch, "E126", {"start": v(-23, -58) * mm, "end": v(-18, -58) * mm});
            skLineSegment(sketch, "E127", {"start": v(-18, -58) * mm, "end": v(-18, -57) * mm});
            skLineSegment(sketch, "E128", {"start": v(-18, -57) * mm, "end": v(-23, -57) * mm});
            skLineSegment(sketch, "E129", {"start": v(-23, -57) * mm, "end": v(-23, -58) * mm});
            skLineSegment(sketch, "E130.0.0", {"start": v(16, -70.1) * mm, "end": v(21, -70.1) * mm});
            skLineSegment(sketch, "E130.0.1", {"start": v(21, -70.1) * mm, "end": v(21, -43.75) * mm});
            skLineSegment(sketch, "E130.0.2", {"start": v(21, -43.75) * mm, "end": v(16, -43.75) * mm});
            skLineSegment(sketch, "E130.0.3", {"start": v(16, -43.75) * mm, "end": v(16, -70.1) * mm});
            skLineSegment(sketch, "E131", {"start": v(16, -43.75) * mm, "end": v(16, -58) * mm});
            skLineSegment(sketch, "E132", {"start": v(16, -58) * mm, "end": v(21, -58) * mm});
            skLineSegment(sketch, "E133", {"start": v(21, -58) * mm, "end": v(21, -57) * mm});
            skLineSegment(sketch, "E134", {"start": v(21, -57) * mm, "end": v(16, -57) * mm});
            skLineSegment(sketch, "E135", {"start": v(16, -57) * mm, "end": v(16, -58) * mm});
            skSolve(sketch);
        }
        {
            var Q0;
            Q0=makeQuery(id+"F28.imprint","IMPRINT",FACE,{"disambiguationData":[TD([[makeQuery(id+"F28.imprint","IMPRINT",EDGE,{"derivedFrom":sQuery(id+"F28.wireOp",EDGE,"E132")}),1.0]])]});
            var Q1;
            Q1=makeQuery(id+"F28.imprint","IMPRINT",FACE,{"disambiguationData":[TD([[makeQuery(id+"F28.imprint","IMPRINT",EDGE,{"derivedFrom":sQuery(id+"F28.wireOp",EDGE,"E126")}),1.0]])]});
            extrude(context, id + "F29", {"entities" : qUnion([Q0, Q1]), "operationType" : NewBodyOperationType.ADD, "depth" : 5 * mm});
        }
        {
            var Q0;
            {var subQ0=sQuery(id+"F22.wireOp",EDGE,"E107");Q0=makeQuery(id+"F22.imprint","IMPRINT",FACE,{"disambiguationData":[TD([[makeQuery(id+"F22.imprint","IMPRINT",EDGE,{"derivedFrom":subQ0}),-1.0]])]});}
            var Q1;
            {var subQ0=sQuery(id+"F22.wireOp",EDGE,"E102");Q1=makeQuery(id+"F22.imprint","IMPRINT",FACE,{"disambiguationData":[TD([[makeQuery(id+"F22.imprint","IMPRINT",EDGE,{"derivedFrom":subQ0}),-1.0]])]});}
            extrude(context, id + "F30", {"entities" : qUnion([Q0, Q1]), "operationType" : NewBodyOperationType.ADD, "depth" : 14.25 * mm});
        }
        {
            var Q0;
            Q0=makeQuery(id+"F30.opExtrude","CAP_FACE",FACE,{"disambiguationData":[OSD([sQuery(id+"F22.wireOp",EDGE,"E102"),sQuery(id+"F22.wireOp",EDGE,"E103"),sQuery(id+"F22.wireOp",EDGE,"E104"),sQuery(id+"F22.wireOp",EDGE,"E105")])],"isStart":false});
            var sketch = newSketch(context, id + "F31", { "sketchPlane" : qUnion([Q0])});
            skLineSegment(sketch, "E136", {"start": v(18, 52.5) * mm, "end": v(18, 47.5) * mm});
            skLineSegment(sketch, "E137", {"start": v(18, 47.5) * mm, "end": v(23, 47.5) * mm});
            skLineSegment(sketch, "E138", {"start": v(23, 47.5) * mm, "end": v(23, 52.5) * mm});
            skLineSegment(sketch, "E139.0.0", {"start": v(-21, 52.5) * mm, "end": v(-21, 51.5) * mm});
            skLineSegment(sketch, "E139.0.1", {"start": v(-21, 51.5) * mm, "end": v(-16, 51.5) * mm});
            skLineSegment(sketch, "E139.0.2", {"start": v(-16, 51.5) * mm, "end": v(-16, 52.5) * mm});
            skLineSegment(sketch, "E139.0.3", {"start": v(-16, 52.5) * mm, "end": v(-21, 52.5) * mm});
            skLineSegment(sketch, "E140", {"start": v(-21, 52.5) * mm, "end": v(-21, 47.5) * mm});
            skLineSegment(sketch, "E141", {"start": v(-21, 47.5) * mm, "end": v(-16, 47.5) * mm});
            skLineSegment(sketch, "E142", {"start": v(-16, 47.5) * mm, "end": v(-16, 52.5) * mm});
            skSolve(sketch);
        }
        {
            var Q0;
            {var subQ2=sQuery(id+"F31.wireOp",EDGE,"E137");Q0=makeQuery(id+"F31.imprint","IMPRINT",FACE,{"disambiguationData":[TD([[makeQuery(id+"F31.imprint","IMPRINT",EDGE,{"derivedFrom":subQ2}),1.0]])]});}
            var Q1;
            {var subQ1=makeQuery(id+"F30.opExtrude","CAP_EDGE",EDGE,{"disambiguationData":[OSD([sQuery(id+"F22.wireOp",EDGE,"E102")])],"isStart":false});Q1=makeQuery(id+"F31.imprint","IMPRINT",FACE,{"disambiguationData":[TD([[makeQuery(id+"F31.imprint","IMPRINT",EDGE,{"derivedFrom":subQ1}),-1.0]])]});}
            var Q2;
            {var subQ0=sQuery(id+"F31.wireOp",EDGE,"E139.0.1");Q2=makeQuery(id+"F31.imprint","IMPRINT",FACE,{"disambiguationData":[TD([[makeQuery(id+"F31.imprint","IMPRINT",EDGE,{"derivedFrom":subQ0}),-1.0]])]});}
            var Q3;
            {var subQ0=sQuery(id+"F31.wireOp",EDGE,"E139.0.1");Q3=makeQuery(id+"F31.imprint","IMPRINT",FACE,{"disambiguationData":[TD([[makeQuery(id+"F31.imprint","IMPRINT",EDGE,{"derivedFrom":subQ0}),1.0]])]});}
            extrude(context, id + "F32", {"entities" : qUnion([Q0, Q1, Q2, Q3]), "operationType" : NewBodyOperationType.ADD, "depth" : 1 * mm});
        }
        {
            var Q0;
            {var subQ0=sQuery(id+"F22.wireOp",EDGE,"E92");var subQ1=sQuery(id+"F0.wireOp",EDGE,"E7");Q0=makeQuery(id+"F32.boolean.opBoolean","MERGE",FACE,{"derivedFrom":[makeQuery(id+"F30.boolean.opBoolean","MERGE",FACE,{"derivedFrom":[makeQuery(id+"F25.boolean.opBoolean","MERGE",FACE,{"derivedFrom":[makeQuery(id+"F23.boolean.opBoolean","MERGE",FACE,{"derivedFrom":[makeQuery(id+"F17.boolean.opBoolean","MERGE",FACE,{"derivedFrom":[makeQuery(id+"F15.boolean.opBoolean","MERGE",FACE,{"derivedFrom":[makeQuery(id+"F1.opExtrude","SWEPT_FACE",FACE,{"disambiguationData":[OSD([subQ1]),TDD([makeQuery(id+"F0.imprint","IMPRINT",EDGE,{"disambiguationData":[TD([[makeQuery(id+"F0.imprint","INTERSECT",VERTEX,{"derivedFrom":[subQ1,sQuery(id+"F0.wireOp",EDGE,"E8")]}),1.0]])],"derivedFrom":subQ1})])]}),makeQuery(id+"F15.opExtrude","SWEPT_FACE",FACE,{"disambiguationData":[OSD([sQuery(id+"F13.wireOp",EDGE,"E51")])]})]}),makeQuery(id+"F17.opExtrude","SWEPT_FACE",FACE,{"disambiguationData":[OSD([sQuery(id+"F16.wireOp",EDGE,"E63")])]})]}),makeQuery(id+"F23.opExtrude","SWEPT_FACE",FACE,{"disambiguationData":[OSD([subQ0])]})]}),makeQuery(id+"F25.opExtrude","SWEPT_FACE",FACE,{"disambiguationData":[OSD([subQ0])]})]}),makeQuery(id+"F29.boolean.opBoolean","MERGE",FACE,{"derivedFrom":[makeQuery(id+"F27.boolean.opBoolean","MERGE",FACE,{"derivedFrom":[makeQuery(id+"F25.opExtrude","SWEPT_FACE",FACE,{"disambiguationData":[OSD([subQ0,sQuery(id+"F22.wireOp",EDGE,"E99")])]}),makeQuery(id+"F27.opExtrude","SWEPT_FACE",FACE,{"disambiguationData":[OSD([sQuery(id+"F26.wireOp",EDGE,"E115"),sQuery(id+"F26.wireOp",EDGE,"E116")])]})]}),makeQuery(id+"F29.opExtrude","SWEPT_FACE",FACE,{"disambiguationData":[OSD([sQuery(id+"F28.wireOp",EDGE,"E129")])]})]}),makeQuery(id+"F30.opExtrude","SWEPT_FACE",FACE,{"disambiguationData":[OSD([sQuery(id+"F22.wireOp",EDGE,"E105")])]})]}),makeQuery(id+"F32.opExtrude","SWEPT_FACE",FACE,{"disambiguationData":[OSD([sQuery(id+"F31.wireOp",EDGE,"E138")])]})]});}
            var sketch = newSketch(context, id + "F33", { "sketchPlane" : qUnion([Q0])});
            skLineSegment(sketch, "E143.0.0", {"start": v(0, 5) * mm, "end": v(0, 21) * mm});
            skLineSegment(sketch, "E143.0.1", {"start": v(0, 21) * mm, "end": v(-0.5, 21) * mm});
            skLineSegment(sketch, "E143.0.2", {"start": v(-0.5, 21) * mm, "end": v(-0.5, 5) * mm});
            skLineSegment(sketch, "E143.0.3", {"start": v(-0.5, 5) * mm, "end": v(0, 5) * mm});
            skLineSegment(sketch, "E144", {"start": v(0, -21) * mm, "end": v(1.5, -21) * mm});
            skLineSegment(sketch, "E145", {"start": v(1.5, -21) * mm, "end": v(1.5, 21) * mm});
            skLineSegment(sketch, "E146", {"start": v(1.5, 21) * mm, "end": v(0, 21) * mm});
            skLineSegment(sketch, "E147", {"start": v(0, 21) * mm, "end": v(0, -21) * mm});
            skSolve(sketch);
        }
        {
            var Q0;
            {var subQ3=sQuery(id+"F33.wireOp",EDGE,"E144");Q0=makeQuery(id+"F33.imprint","IMPRINT",FACE,{"disambiguationData":[TD([[makeQuery(id+"F33.imprint","IMPRINT",EDGE,{"derivedFrom":subQ3}),1.0]])]});}
            extrude(context, id + "F34", {"entities" : qUnion([Q0]), "operationType" : NewBodyOperationType.ADD, "oppositeDirection" : true, "depth" : 0.5 * mm});
        }
        {
            var Q0;
            Q0=makeQuery(id+"F34.opExtrude","SWEPT_FACE",FACE,{"disambiguationData":[OSD([sQuery(id+"F33.wireOp",EDGE,"E145")])]});
            var sketch = newSketch(context, id + "F35", { "sketchPlane" : qUnion([Q0])});
            skLineSegment(sketch, "E148", {"start": v(-22.5, -21) * mm, "end": v(-21.5, -21) * mm});
            skLineSegment(sketch, "E149", {"start": v(-21.5, -21) * mm, "end": v(-21.5, 21) * mm});
            skLineSegment(sketch, "E150", {"start": v(-21.5, 21) * mm, "end": v(-22.5, 21) * mm});
            skSolve(sketch);
        }
        {
            var Q0;
            Q0=makeQuery(id+"F35.imprint","IMPRINT",FACE,{"disambiguationData":[TD([[makeQuery(id+"F35.imprint","IMPRINT",EDGE,{"derivedFrom":sQuery(id+"F35.wireOp",EDGE,"E148")}),1.0]])]});
            extrude(context, id + "F36", {"entities" : qUnion([Q0]), "operationType" : NewBodyOperationType.ADD, "oppositeDirection" : true, "depth" : 0.5 * mm});
        }
        {
            var Q0;
            {var subQ0=sQuery(id+"F0.wireOp",EDGE,"E9");Q0=makeQuery(id+"F1.opExtrude","SWEPT_FACE",FACE,{"disambiguationData":[OSD([subQ0]),TDD([makeQuery(id+"F0.imprint","IMPRINT",EDGE,{"disambiguationData":[TD([[makeQuery(id+"F0.imprint","INTERSECT",VERTEX,{"derivedFrom":[sQuery(id+"F0.wireOp",EDGE,"E6"),subQ0]}),1.0]])],"derivedFrom":subQ0})])]});}
            var sketch = newSketch(context, id + "F37", { "sketchPlane" : qUnion([Q0])});
            skLineSegment(sketch, "E151.0.0", {"start": v(15, -21) * mm, "end": v(15, -43.75) * mm});
            skLineSegment(sketch, "E151.0.1", {"start": v(15, -43.75) * mm, "end": v(51.5, -43.75) * mm});
            skLineSegment(sketch, "E151.0.2", {"start": v(51.5, -43.75) * mm, "end": v(51.5, -57) * mm});
            skLineSegment(sketch, "E151.0.3", {"start": v(51.5, -57) * mm, "end": v(47.5, -57) * mm});
            skLineSegment(sketch, "E151.0.4", {"start": v(47.5, -57) * mm, "end": v(47.5, -58) * mm});
            skLineSegment(sketch, "E151.0.5", {"start": v(47.5, -58) * mm, "end": v(52.5, -58) * mm});
            skLineSegment(sketch, "E151.0.6", {"start": v(52.5, -58) * mm, "end": v(52.5, -43.75) * mm});
            skLineSegment(sketch, "E151.0.7", {"start": v(52.5, -43.75) * mm, "end": v(89, -43.75) * mm});
            skLineSegment(sketch, "E151.0.8", {"start": v(89, -43.75) * mm, "end": v(89, -57) * mm});
            skLineSegment(sketch, "E151.0.9", {"start": v(89, -57) * mm, "end": v(84, -57) * mm});
            skLineSegment(sketch, "E151.0.10", {"start": v(84, -57) * mm, "end": v(84, -58) * mm});
            skLineSegment(sketch, "E151.0.11", {"start": v(84, -58) * mm, "end": v(89, -58) * mm});
            skLineSegment(sketch, "E151.0.12", {"start": v(89, -58) * mm, "end": v(89, -70.1) * mm});
            skLineSegment(sketch, "E151.0.13", {"start": v(89, -70.1) * mm, "end": v(90, -70.1) * mm});
            skLineSegment(sketch, "E151.0.14", {"start": v(90, -70.1) * mm, "end": v(90, -42.75) * mm});
            skLineSegment(sketch, "E151.0.15", {"start": v(90, -42.75) * mm, "end": v(16, -42.75) * mm});
            skLineSegment(sketch, "E151.0.16", {"start": v(16, -42.75) * mm, "end": v(16, -13) * mm});
            skLineSegment(sketch, "E151.0.17", {"start": v(16, -13) * mm, "end": v(15, -13) * mm});
            skLineSegment(sketch, "E151.0.18", {"start": v(15, -13) * mm, "end": v(15, -20) * mm});
            skLineSegment(sketch, "E151.0.19", {"start": v(15, -20) * mm, "end": v(0.5, -20) * mm});
            skLineSegment(sketch, "E151.0.20", {"start": v(0.5, -20) * mm, "end": v(0.5, -5) * mm});
            skLineSegment(sketch, "E151.0.21", {"start": v(0.5, -5) * mm, "end": v(0, -5) * mm});
            skLineSegment(sketch, "E151.0.22", {"start": v(0, -5) * mm, "end": v(0, -21) * mm});
            skLineSegment(sketch, "E151.0.23", {"start": v(0, -21) * mm, "end": v(15, -21) * mm});
            skLineSegment(sketch, "E152", {"start": v(-1.5, 21) * mm, "end": v(-1.5, -21) * mm});
            skLineSegment(sketch, "E153", {"start": v(-1.5, -21) * mm, "end": v(0, -21) * mm});
            skLineSegment(sketch, "E154", {"start": v(0, -21) * mm, "end": v(0, 21) * mm});
            skLineSegment(sketch, "E155", {"start": v(-1.5, 21) * mm, "end": v(0, 21) * mm});
            skSolve(sketch);
        }
        {
            var Q0;
            Q0=makeQuery(id+"F37.imprint","IMPRINT",FACE,{"disambiguationData":[TD([[makeQuery(id+"F37.imprint","IMPRINT",EDGE,{"derivedFrom":sQuery(id+"F37.wireOp",EDGE,"E152")}),1.0]])]});
            extrude(context, id + "F38", {"entities" : qUnion([Q0]), "operationType" : NewBodyOperationType.ADD, "oppositeDirection" : true, "depth" : 0.5 * mm});
        }
        {
            var Q0;
            Q0=makeQuery(id+"F38.opExtrude","SWEPT_FACE",FACE,{"disambiguationData":[OSD([sQuery(id+"F37.wireOp",EDGE,"E152")])]});
            var sketch = newSketch(context, id + "F39", { "sketchPlane" : qUnion([Q0])});
            skLineSegment(sketch, "E156", {"start": v(21, 21) * mm, "end": v(19.5, 21) * mm});
            skLineSegment(sketch, "E157", {"start": v(19.5, 21) * mm, "end": v(19.5, -21) * mm});
            skLineSegment(sketch, "E158", {"start": v(19.5, -21) * mm, "end": v(21, -21) * mm});
            skLineSegment(sketch, "E159", {"start": v(21, -21) * mm, "end": v(21, 21) * mm});
            skSolve(sketch);
        }
        {
            var Q0;
            {var subQ0=sQuery(id+"F39.wireOp",EDGE,"E159");Q0=makeQuery(id+"F39.imprint","IMPRINT",FACE,{"disambiguationData":[TD([[makeQuery(id+"F39.imprint","IMPRINT",EDGE,{"derivedFrom":subQ0}),-1.0]])]});}
            var Q1;
            {var subQ2=sQuery(id+"F39.wireOp",EDGE,"E157");Q1=makeQuery(id+"F39.imprint","IMPRINT",FACE,{"disambiguationData":[TD([[makeQuery(id+"F39.imprint","IMPRINT",EDGE,{"derivedFrom":subQ2}),1.0]])]});}
            extrude(context, id + "F40", {"entities" : qUnion([Q0, Q1]), "operationType" : NewBodyOperationType.ADD, "depth" : 0.5 * mm});
        }
    });
